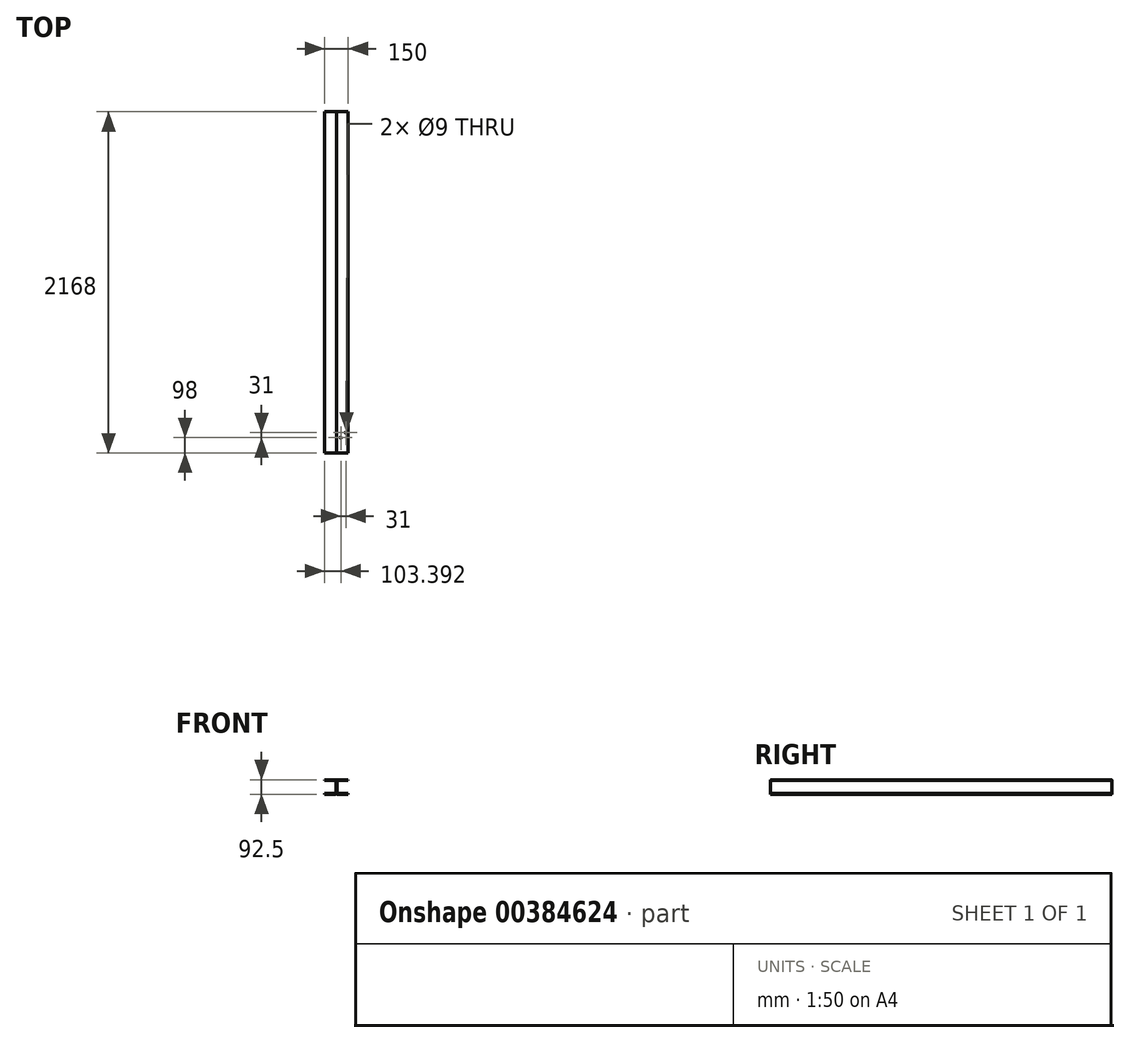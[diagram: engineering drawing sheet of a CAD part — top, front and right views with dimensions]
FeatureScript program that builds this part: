
annotation { "Feature Type Name" : "Feature", "Feature Type Description" : "" }
export const myFeature = defineFeature(function(context is Context, id is Id, definition is map)
    precondition{}
    {
        {
            var Q0;
            Q0=qCreatedBy(makeId("Front.planeOp"),FACE);
            var sketch = newSketch(context, id + "F0", { "sketchPlane" : qUnion([Q0])});
            skLineSegment(sketch, "E0.bottom", {"start": v(-75, -46.25) * mm, "end": v(-8, -46.25) * mm});
            skLineSegment(sketch, "E0.top", {"start": v(-75, 46.25) * mm, "end": v(-8, 46.25) * mm});
            skLineSegment(sketch, "E0.left", {"start": v(-75, -46.25) * mm, "end": v(-75, -42.25) * mm});
            skLineSegment(sketch, "E0.right", {"start": v(75, -46.25) * mm, "end": v(75, -42.25) * mm});
            skPoint(sketch, "E0.middle", {"position": v(0, 0) * mm});
            skLineSegment(sketch, "E1.bottom", {"start": v(-75, -42.25) * mm, "end": v(-8, -42.25) * mm});
            skLineSegment(sketch, "E1.top", {"start": v(-75, 42.25) * mm, "end": v(-8, 42.25) * mm});
            skLineSegment(sketch, "E1.right", {"start": v(-4, -38.25) * mm, "end": v(-4, 38.25) * mm});
            skPoint(sketch, "E1.middle", {"position": v(-37.5, 0) * mm});
            skLineSegment(sketch, "E2.bottom", {"start": v(8, -42.25) * mm, "end": v(75, -42.25) * mm});
            skLineSegment(sketch, "E2.top", {"start": v(8, 42.25) * mm, "end": v(75, 42.25) * mm});
            skLineSegment(sketch, "E2.left", {"start": v(4, -38.25) * mm, "end": v(4, 38.25) * mm});
            skPoint(sketch, "E2.middle", {"position": v(37.5, 0) * mm});
            skPoint(sketch, "E1.left.end.orphan", {"position": v(-71, 42.25) * mm});
            skPoint(sketch, "E1.left.start.orphan", {"position": v(-71, -42.25) * mm});
            skLineSegment(sketch, "E3.trimOffspring", {"start": v(-75, 42.25) * mm, "end": v(-75, 46.25) * mm});
            skPoint(sketch, "E2.right.end.orphan", {"position": v(71, 42.25) * mm});
            skPoint(sketch, "E2.right.start.orphan", {"position": v(71, -42.25) * mm});
            skLineSegment(sketch, "E4.trimOffspring", {"start": v(75, 42.25) * mm, "end": v(75, 46.25) * mm});
            skLineSegment(sketch, "E5", {"start": v(0, -38.25) * mm, "end": v(0, 38.25) * mm});
            skPoint(sketch, "E6.visualSharp", {"position": v(-4, 42.25) * mm});
            skArc(sketch, "E6.filletArc", {"start": v(-4, 38.25) * mm, "mid": v(-5.17, 41.08) * mm, "end": v(-8, 42.25) * mm});
            skPoint(sketch, "E7.visualSharp", {"position": v(4, 42.25) * mm});
            skArc(sketch, "E7.filletArc", {"start": v(8, 42.25) * mm, "mid": v(5.17, 41.08) * mm, "end": v(4, 38.25) * mm});
            skPoint(sketch, "E8.visualSharp", {"position": v(4, -42.25) * mm});
            skArc(sketch, "E8.filletArc", {"start": v(4, -38.25) * mm, "mid": v(5.17, -41.08) * mm, "end": v(8, -42.25) * mm});
            skPoint(sketch, "E9.visualSharp", {"position": v(-4, -42.25) * mm});
            skArc(sketch, "E9.filletArc", {"start": v(-8, -42.25) * mm, "mid": v(-5.17, -41.08) * mm, "end": v(-4, -38.25) * mm});
            skPoint(sketch, "E10.newPointA", {"position": v(75, 46.25) * mm});
            skPoint(sketch, "E10.newPointB", {"position": v(0, 46.25) * mm});
            skArc(sketch, "E10.filletArc", {"start": v(0, 38.25) * mm, "mid": v(-2.34, 43.9) * mm, "end": v(-8, 46.25) * mm});
            skLineSegment(sketch, "E11", {"start": v(8, 46.25) * mm, "end": v(75, 46.25) * mm});
            skLineSegment(sketch, "E12", {"start": v(0, 38.25) * mm, "end": v(0, 38.25) * mm});
            skArc(sketch, "E13.filletArc", {"start": v(8, 46.25) * mm, "mid": v(2.34, 43.9) * mm, "end": v(0, 38.25) * mm});
            skPoint(sketch, "E14.newPointA", {"position": v(75, -46.25) * mm});
            skPoint(sketch, "E14.newPointB", {"position": v(0, -46.25) * mm});
            skArc(sketch, "E14.filletArc", {"start": v(-8, -46.25) * mm, "mid": v(-2.34, -43.9) * mm, "end": v(0, -38.25) * mm});
            skLineSegment(sketch, "E15", {"start": v(0, -38.25) * mm, "end": v(0, -38.25) * mm});
            skLineSegment(sketch, "E16", {"start": v(8, -46.25) * mm, "end": v(75, -46.25) * mm});
            skArc(sketch, "E17.filletArc", {"start": v(0, -38.25) * mm, "mid": v(2.34, -43.9) * mm, "end": v(8, -46.25) * mm});
            skSolve(sketch);
        }
        {
            var Q0;
            Q0=makeQuery(id+"F0.imprint","IMPRINT",FACE,{"disambiguationData":[TD([[makeQuery(id+"F0.imprint","IMPRINT",EDGE,{"derivedFrom":sQuery(id+"F0.wireOp",EDGE,"E0.right")}),1.0]])]});
            var Q1;
            Q1=makeQuery(id+"F0.imprint","IMPRINT",FACE,{"disambiguationData":[TD([[makeQuery(id+"F0.imprint","IMPRINT",EDGE,{"derivedFrom":sQuery(id+"F0.wireOp",EDGE,"E0.bottom")}),1.0]])]});
            extrude(context, id + "F1", {"entities" : qUnion([Q0, Q1]), "oppositeDirection" : true, "depth" : 2168 * mm});
        }
        {
            var Q0;
            Q0=qCreatedBy(makeId("Top.planeOp"),FACE);
            cPlane(context, id + "F2", {"entities" : qUnion([Q0]), "cplaneType" : CPlaneType.OFFSET, "offset" : 46.25 * mm, "width" : 150 * mm, "height" : 150 * mm});
        }
        {
            var Q0;
            Q0=qCreatedBy(id+"F2.planeOp",FACE);
            var sketch = newSketch(context, id + "F3", { "sketchPlane" : qUnion([Q0])});
            skLineSegment(sketch, "E18", {"start": v(414.85, 0) * mm, "end": v(532.46, 0) * mm});
            skLineSegment(sketch, "E19", {"start": v(532.46, 0) * mm, "end": v(532.46, 14.5) * mm});
            skLineSegment(sketch, "E20", {"start": v(532.46, 14.5) * mm, "end": v(504.52, 14.5) * mm});
            skLineSegment(sketch, "E21", {"start": v(504.52, 14.5) * mm, "end": v(504.52, 60.11) * mm});
            skLineSegment(sketch, "E22", {"start": v(504.52, 60.11) * mm, "end": v(461.6, 60.11) * mm});
            skLineSegment(sketch, "E23", {"start": v(0, 0) * mm, "end": v(28.4, 0) * mm});
            skLineSegment(sketch, "E24", {"start": v(28.4, 0) * mm, "end": v(28.4, 98) * mm});
            skLineSegment(sketch, "E25", {"start": v(28.4, 98) * mm, "end": v(28.4, 129) * mm});
            skLineSegment(sketch, "E26", {"start": v(28.4, 129) * mm, "end": v(59.4, 129) * mm});
            skCircle(sketch, "E27", {"center": v(28.4, 98) * mm, "radius": 4.5 * mm});
            skCircle(sketch, "E28", {"center": v(59.4, 129) * mm, "radius": 4.5 * mm});
            skCircle(sketch, "E29.MirrorC", {"center": v(-59.4, 129) * mm, "radius": 4.5 * mm});
            skCircle(sketch, "E30.MirrorC", {"center": v(-28.4, 98) * mm, "radius": 4.5 * mm});
            skSolve(sketch);
        }
        {
            var Q0;
            Q0=makeQuery(id+"F3.imprint","IMPRINT",FACE,{"disambiguationData":[TD([[makeQuery(id+"F3.imprint","IMPRINT",EDGE,{"derivedFrom":sQuery(id+"F3.wireOp",EDGE,"E28")}),1.0]])]});
            var Q1;
            {var subQ0=sQuery(id+"F3.wireOp",EDGE,"E25");var subQ1=sQuery(id+"F3.wireOp",EDGE,"E24");var subQ2=makeQuery(id+"F3.imprint","INTERSECT",VERTEX,{"derivedFrom":[subQ1,subQ0]});Q1=makeQuery(id+"F3.imprint","IMPRINT",FACE,{"disambiguationData":[TD([[makeQuery(id+"F3.imprint","IMPRINT",EDGE,{"disambiguationData":[TD([[subQ2,1.0]])],"derivedFrom":subQ1}),-1.0]])]});}
            var Q2;
            {var subQ0=sQuery(id+"F3.wireOp",EDGE,"E25");var subQ1=sQuery(id+"F3.wireOp",EDGE,"E24");var subQ2=makeQuery(id+"F3.imprint","INTERSECT",VERTEX,{"derivedFrom":[subQ1,subQ0]});Q2=makeQuery(id+"F3.imprint","IMPRINT",FACE,{"disambiguationData":[TD([[makeQuery(id+"F3.imprint","IMPRINT",EDGE,{"disambiguationData":[TD([[subQ2,1.0]])],"derivedFrom":subQ1}),1.0]])]});}
            var Q3;
            Q3=makeQuery(id+"F3.imprint","IMPRINT",FACE,{"disambiguationData":[TD([[makeQuery(id+"F3.imprint","IMPRINT",EDGE,{"derivedFrom":sQuery(id+"F3.wireOp",EDGE,"E30.MirrorC")}),-1.0]])]});
            var Q4;
            Q4=makeQuery(id+"F3.imprint","IMPRINT",FACE,{"disambiguationData":[TD([[makeQuery(id+"F3.imprint","IMPRINT",EDGE,{"derivedFrom":sQuery(id+"F3.wireOp",EDGE,"E29.MirrorC")}),-1.0]])]});
            extrude(context, id + "F4", {"entities" : qUnion([Q0, Q1, Q2, Q3, Q4]), "operationType" : NewBodyOperationType.REMOVE, "oppositeDirection" : true, "depth" : 4 * mm});
        }
    });
